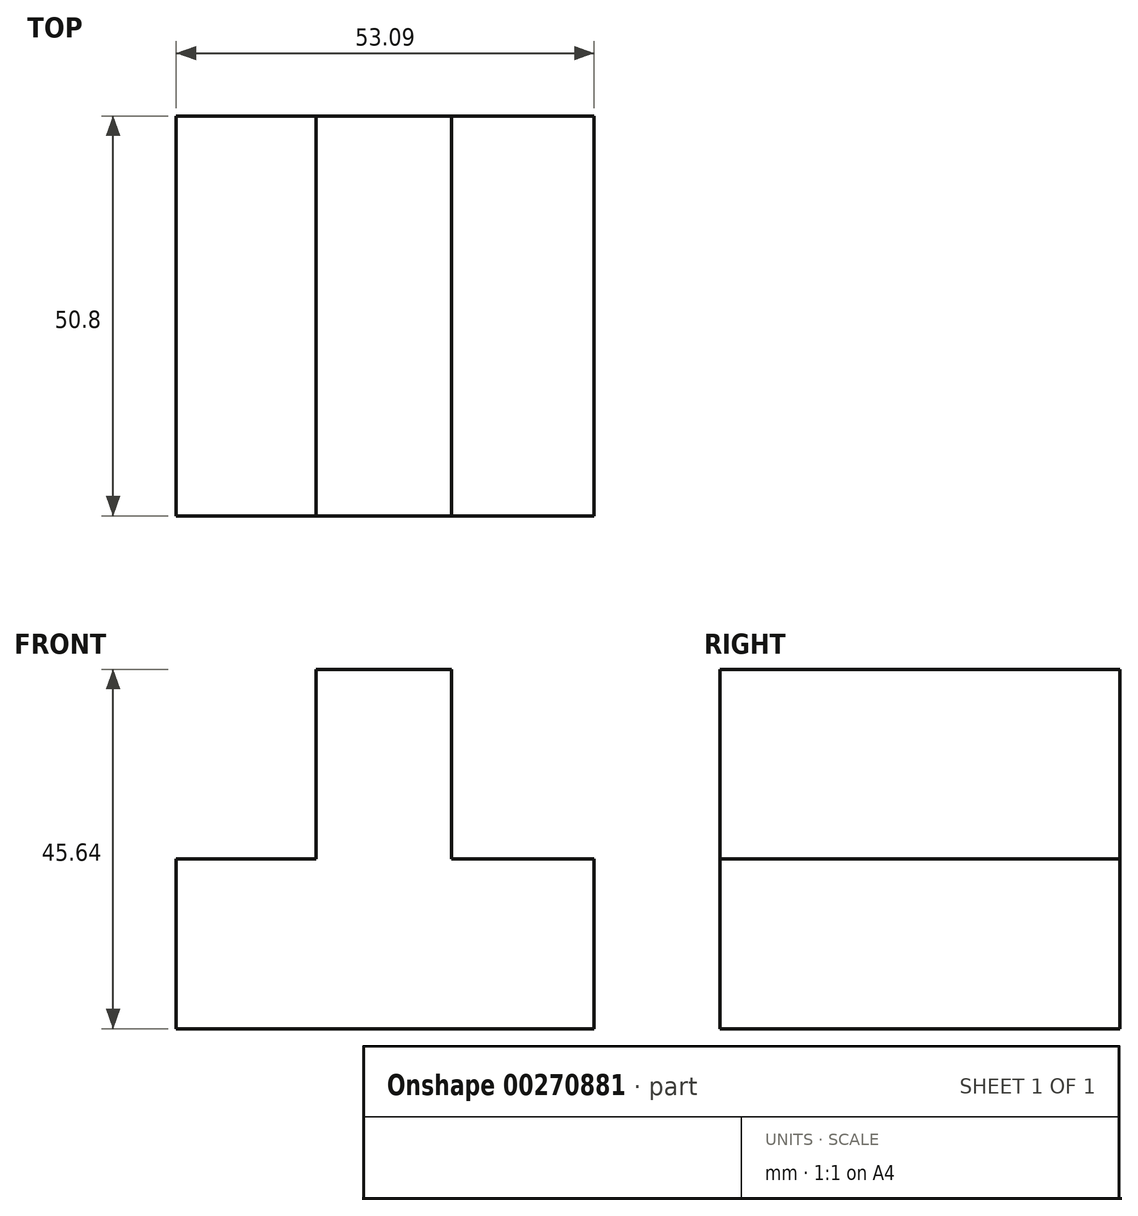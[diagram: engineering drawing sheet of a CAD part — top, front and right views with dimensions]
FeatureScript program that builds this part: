
annotation { "Feature Type Name" : "Feature", "Feature Type Description" : "" }
export const myFeature = defineFeature(function(context is Context, id is Id, definition is map)
    precondition{}
    {
        {
            var Q0;
            Q0=qCreatedBy(makeId("Front.planeOp"),FACE);
            var sketch = newSketch(context, id + "F0", { "sketchPlane" : qUnion([Q0])});
            skLineSegment(sketch, "E0.bottom", {"start": v(-53.09, 0) * mm, "end": v(0, 0) * mm});
            skLineSegment(sketch, "E0.top", {"start": v(-53.09, 0) * mm, "end": v(0, 0) * mm});
            skLineSegment(sketch, "E0.left", {"start": v(-53.09, 0) * mm, "end": v(-53.09, 0) * mm});
            skLineSegment(sketch, "E0.right", {"start": v(0, 0) * mm, "end": v(0, 0) * mm});
            skLineSegment(sketch, "E1.top", {"start": v(0, 21.58) * mm, "end": v(0, 21.58) * mm});
            skLineSegment(sketch, "E1.left", {"start": v(0, 0) * mm, "end": v(0, 21.58) * mm});
            skLineSegment(sketch, "E1.right", {"start": v(0, 0) * mm, "end": v(0, 21.58) * mm});
            skLineSegment(sketch, "E2.bottom", {"start": v(0, 21.58) * mm, "end": v(-18.14, 21.58) * mm});
            skLineSegment(sketch, "E2.top", {"start": v(0, 21.58) * mm, "end": v(-18.14, 21.58) * mm});
            skLineSegment(sketch, "E2.right", {"start": v(-18.14, 21.58) * mm, "end": v(-18.14, 21.58) * mm});
            skLineSegment(sketch, "E3.top", {"start": v(-53.09, 21.58) * mm, "end": v(-53.09, 21.58) * mm});
            skLineSegment(sketch, "E3.left", {"start": v(-53.09, 0) * mm, "end": v(-53.09, 21.58) * mm});
            skLineSegment(sketch, "E3.right", {"start": v(-53.09, 0) * mm, "end": v(-53.09, 21.58) * mm});
            skLineSegment(sketch, "E4.bottom", {"start": v(-35.33, 21.58) * mm, "end": v(-53.09, 21.58) * mm});
            skLineSegment(sketch, "E4.top", {"start": v(-35.33, 21.58) * mm, "end": v(-53.09, 21.58) * mm});
            skLineSegment(sketch, "E4.left", {"start": v(-35.33, 21.58) * mm, "end": v(-35.33, 21.58) * mm});
            skLineSegment(sketch, "E5.top", {"start": v(-35.33, 45.64) * mm, "end": v(-35.33, 45.64) * mm});
            skLineSegment(sketch, "E5.left", {"start": v(-35.33, 21.58) * mm, "end": v(-35.33, 45.64) * mm});
            skLineSegment(sketch, "E5.right", {"start": v(-35.33, 21.58) * mm, "end": v(-35.33, 45.64) * mm});
            skLineSegment(sketch, "E6.bottom", {"start": v(-18.14, 45.64) * mm, "end": v(-35.33, 45.64) * mm});
            skLineSegment(sketch, "E6.top", {"start": v(-18.14, 45.64) * mm, "end": v(-35.33, 45.64) * mm});
            skLineSegment(sketch, "E6.left", {"start": v(-18.14, 45.64) * mm, "end": v(-18.14, 45.64) * mm});
            skLineSegment(sketch, "E7.left", {"start": v(-18.14, 45.64) * mm, "end": v(-18.14, 21.58) * mm});
            skLineSegment(sketch, "E7.right", {"start": v(-18.14, 45.64) * mm, "end": v(-18.14, 21.58) * mm});
            skSolve(sketch);
        }
        {
            var Q0;
            Q0 = qSketchRegion(id + "F0", true);
            extrude(context, id + "F1", {"entities" : qUnion([Q0]), "depth" : 50.8 * mm});
        }
    });
